# Revit family: НЕВАТОМ_Щиты приточные, водяной калорифер W, Версия 1
name_source: partatom
category: Электрооборудование
revit_build: Autodesk Revit 2017 (Build: 20170118_1100(x64)
units: mm (PartAtom-declared; Revit-internal decimal feet)

## family parameters
Всегда вертикально = Да
Конфигурация панели = Два столбца, слева направо
На основе рабочей плоскости = Нет
Общий = Нет
При загрузке вырезать с полостями = Нет
Размер круглого соединителя = Использовать диаметр
Тип детали = Щит
Точка расчета площади = Нет

## types (14) — shared parameters
ADSK_Единица измерения = шт.
ADSK_Завод-изготовитель = НЕВАТОМ
ADSK_Количество = 1
ADSK_Размер_Высота = 410 мм
ADSK_Размер_Длина = 300 мм
ADSK_Размер_Ширина = 153 мм

## per-type parameters (varying)
| type | ADSK_Марка | ADSK_Наименование | ADSK_Напряжение | НЕВАТОМ_Номинальный ток двигателя | НЕВАТОМ_Ориентировочная мощность двигателя | НЕВАТОМ_Преобразователь частоты Danfoss, кВт | НЕВАТОМ_Симисторный регулятор |
| ABU–W–1–ZM–0,35 | ABU–W–1–ZM–0,35 | ABU–W–1–ZM–0,35 | 380 В | 2 А | 0 кВт | ND-051 0,37 кВт для 3 фазы |  |
| ABU–W–1–ZM–0,75 | ABU–W–1–ZM–0,75 | ABU–W–1–ZM–0,75 | 380 В | 3 А | 1 кВт | ND-051 0,75 кВт для 3 фазы |  |
| ABU–W–1–ZM–1,5 | ABU–W–1–ZM–1,5 | ABU–W–1–ZM–1,5 | 380 В | 4 А | 2 кВт | ND-051 1.5 кВт для 3 фазы |  |
| ABU–W–1–ZM–2,2 | ABU–W–1–ZM–2,2 | ABU–W–1–ZM–2,2 | 380 В | 6 А | 2 кВт | ND-051 2.2 кВт для 3 фазы |  |
| ABU–W–1–ZM–3,0 | ABU–W–1–ZM–3,0 | ABU–W–1–ZM–3,0 | 380 В | 10 А | 3 кВт | ND-051 3,0 кВт для 3 фазы |  |
| ABU–W–1–ZM–4,0 | ABU–W–1–ZM–4,0 | ABU–W–1–ZM–4,0 | 380 В | 10 А | 4 кВт | ND-051 4,0 кВт для 3 фазы |  |
| ABU–W–1–ZM–5,5 | ABU–W–1–ZM–5,5 | ABU–W–1–ZM–5,5 | 380 В | 13 А | 6 кВт | ND-051 5,5 кВт для 3 фазы |  |
| ABU–W–1–ZM–7,5 | ABU–W–1–ZM–7,5 | ABU–W–1–ZM–7,5 | 380 В | 18 А | 8 кВт | ND-051 7,5 кВт для 3 фазы |  |
| ABU–W–1–ZM–11,0 | ABU–W–1–ZM–7,5 | ABU–W–1–ZM–7,5 | 380 В | 24 А | 11 кВт | ND-051 11,0 кВт для 3 фазы |  |
| ABU–W–1–ZM–15,0 | ABU–W–1–ZM–15,0 | ABU–W–1–ZM–15,0 | 380 В | 32 А | 15 кВт | ND-051 15,0 кВт для 3 фазы |  |
| ABU–W–1–Z–0,35e–PZ/UVi | ABU–W–1–Z–0,35e–PZ/UVi | ABU–W–1–Z–0,35e–PZ/UVi | 220 В | 2 А | 0 кВт |  | SRM 2,5 |
| ABU–W–1–Z–0,5e–PZ/UVi | ABU–W–1–Z–0,5e–PZ/UVi | ABU–W–1–Z–0,5e–PZ/UVi | 220 В | 3 А | 1 кВт |  | SRM 2,5 |
| ABU–W–1–Z–0,8e–PZ/UVi | ABU–W–1–Z–0,8e–PZ/UVi | ABU–W–1–Z–0,8e–PZ/UVi | 220 В | 3 А | 1 кВт |  | SRM 5 |
| ABU–W–1–Z–1,0e–PZ/UVi | ABU–W–1–Z–1,0e–PZ/UVi | ABU–W–1–Z–1,0e–PZ/UVi | 220 В | 5 А | 1 кВт |  | SRM 5 |
